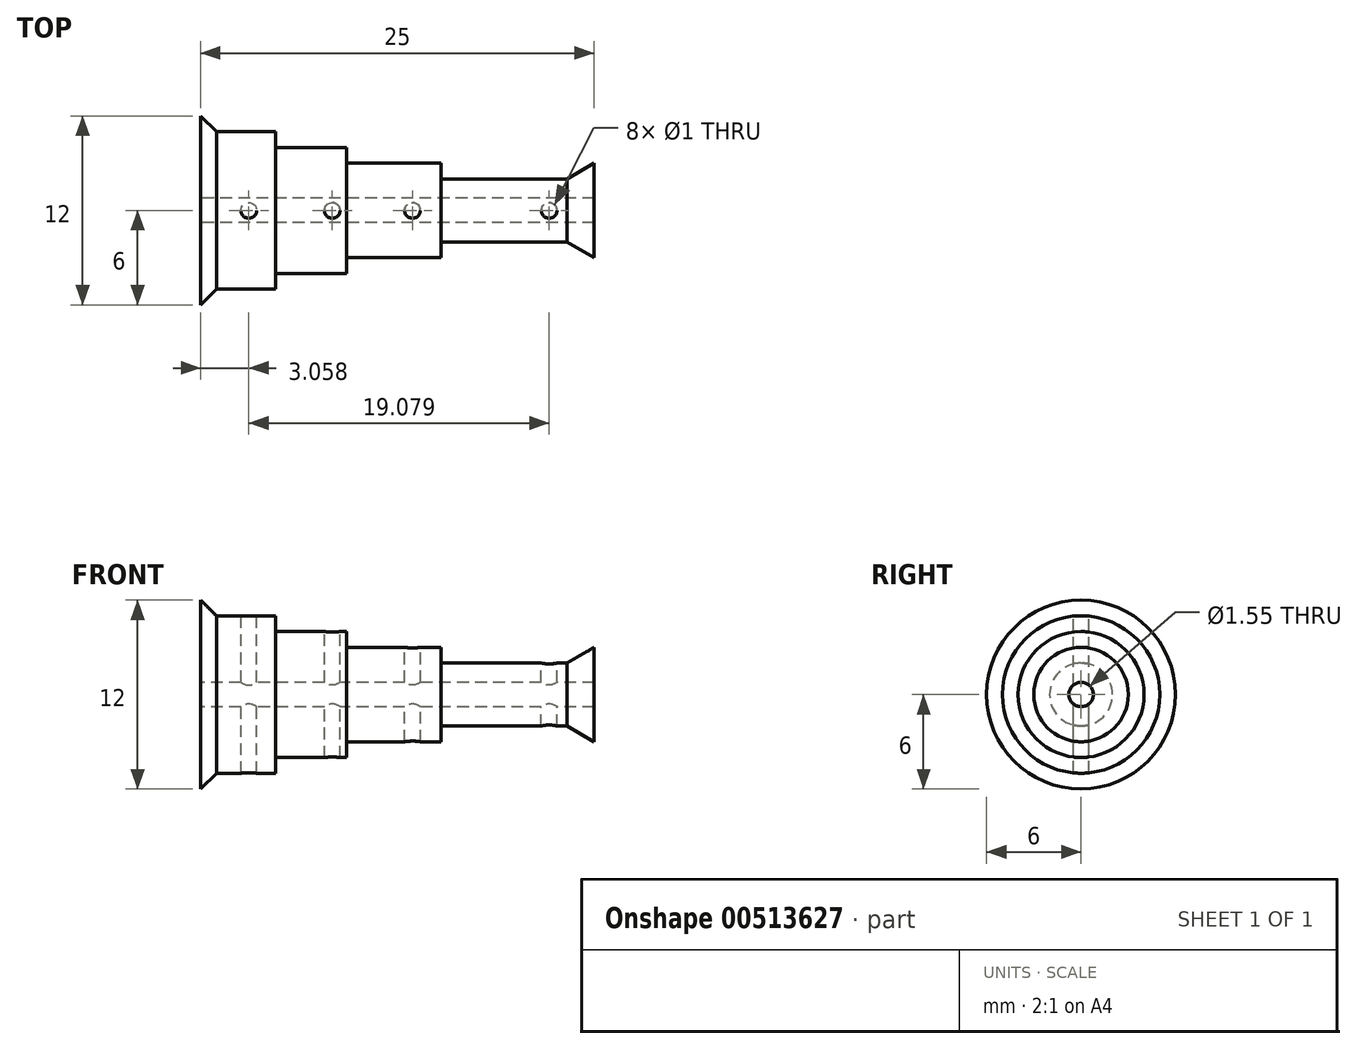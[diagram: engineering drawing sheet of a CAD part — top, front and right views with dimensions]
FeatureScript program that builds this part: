
annotation { "Feature Type Name" : "Feature", "Feature Type Description" : "" }
export const myFeature = defineFeature(function(context is Context, id is Id, definition is map)
    precondition{}
    {
        {
            var Q0;
            Q0=qCreatedBy(makeId("Front.planeOp"),FACE);
            var sketch = newSketch(context, id + "F0", { "sketchPlane" : qUnion([Q0])});
            skLineSegment(sketch, "E0", {"start": v(-22.67, 0) * mm, "end": v(34.76, 0) * mm, "construction": true});
            skLineSegment(sketch, "E1", {"start": v(0, 6) * mm, "end": v(0, 0) * mm});
            skLineSegment(sketch, "E2", {"start": v(0, 0) * mm, "end": v(0, 6) * mm});
            skLineSegment(sketch, "E3", {"start": v(25, 3) * mm, "end": v(25, 0) * mm});
            skLineSegment(sketch, "E4", {"start": v(0, 0.78) * mm, "end": v(25, 0.78) * mm});
            skLineSegment(sketch, "E5", {"start": v(23.27, 2) * mm, "end": v(25, 3) * mm});
            skLineSegment(sketch, "E6", {"start": v(25, 3) * mm, "end": v(25, 3) * mm});
            skLineSegment(sketch, "E7", {"start": v(1, 5) * mm, "end": v(4.77, 5) * mm});
            skLineSegment(sketch, "E8", {"start": v(15.27, 2) * mm, "end": v(23.27, 2) * mm});
            skLineSegment(sketch, "E9", {"start": v(1, 5) * mm, "end": v(0, 6) * mm});
            skLineSegment(sketch, "E10", {"start": v(4.77, 5) * mm, "end": v(4.77, 4) * mm});
            skLineSegment(sketch, "E11", {"start": v(4.77, 4) * mm, "end": v(9.27, 4) * mm});
            skLineSegment(sketch, "E12", {"start": v(9.27, 4) * mm, "end": v(9.27, 3) * mm});
            skLineSegment(sketch, "E13", {"start": v(9.27, 3) * mm, "end": v(15.27, 3) * mm});
            skLineSegment(sketch, "E14", {"start": v(15.27, 3) * mm, "end": v(15.27, 2) * mm});
            skSolve(sketch);
        }
        {
            var Q0;
            Q0=qSketchRegion(id+"F0",true);
            var Q1;
            Q1=sQuery(id+"F0.wireOp",EDGE,"E0");
            revolve(context, id + "F1", {"entities" : qUnion([Q0]), "axis" : qUnion([Q1]), "revolveType" : RevolveType.FULL});
        }
        {
            var Q0;
            Q0=qCreatedBy(makeId("Top.planeOp"),FACE);
            var sketch = newSketch(context, id + "F2", { "sketchPlane" : qUnion([Q0])});
            skCircle(sketch, "E15", {"center": v(3.06, 0) * mm, "radius": 0.5 * mm});
            skCircle(sketch, "E16", {"center": v(8.36, 0) * mm, "radius": 0.5 * mm});
            skCircle(sketch, "E17", {"center": v(13.46, 0) * mm, "radius": 0.5 * mm});
            skCircle(sketch, "E18", {"center": v(22.14, 0) * mm, "radius": 0.5 * mm});
            skSolve(sketch);
        }
        {
            var Q0;
            Q0 = qSketchRegion(id + "F2", true);
            extrude(context, id + "F3", {"entities" : qUnion([Q0]), "operationType" : NewBodyOperationType.REMOVE, "endBound" : BoundingType.SYMMETRIC, "oppositeDirection" : true, "depth" : 25 * mm, "offsetDistance" : 25 * mm});
        }
    });
